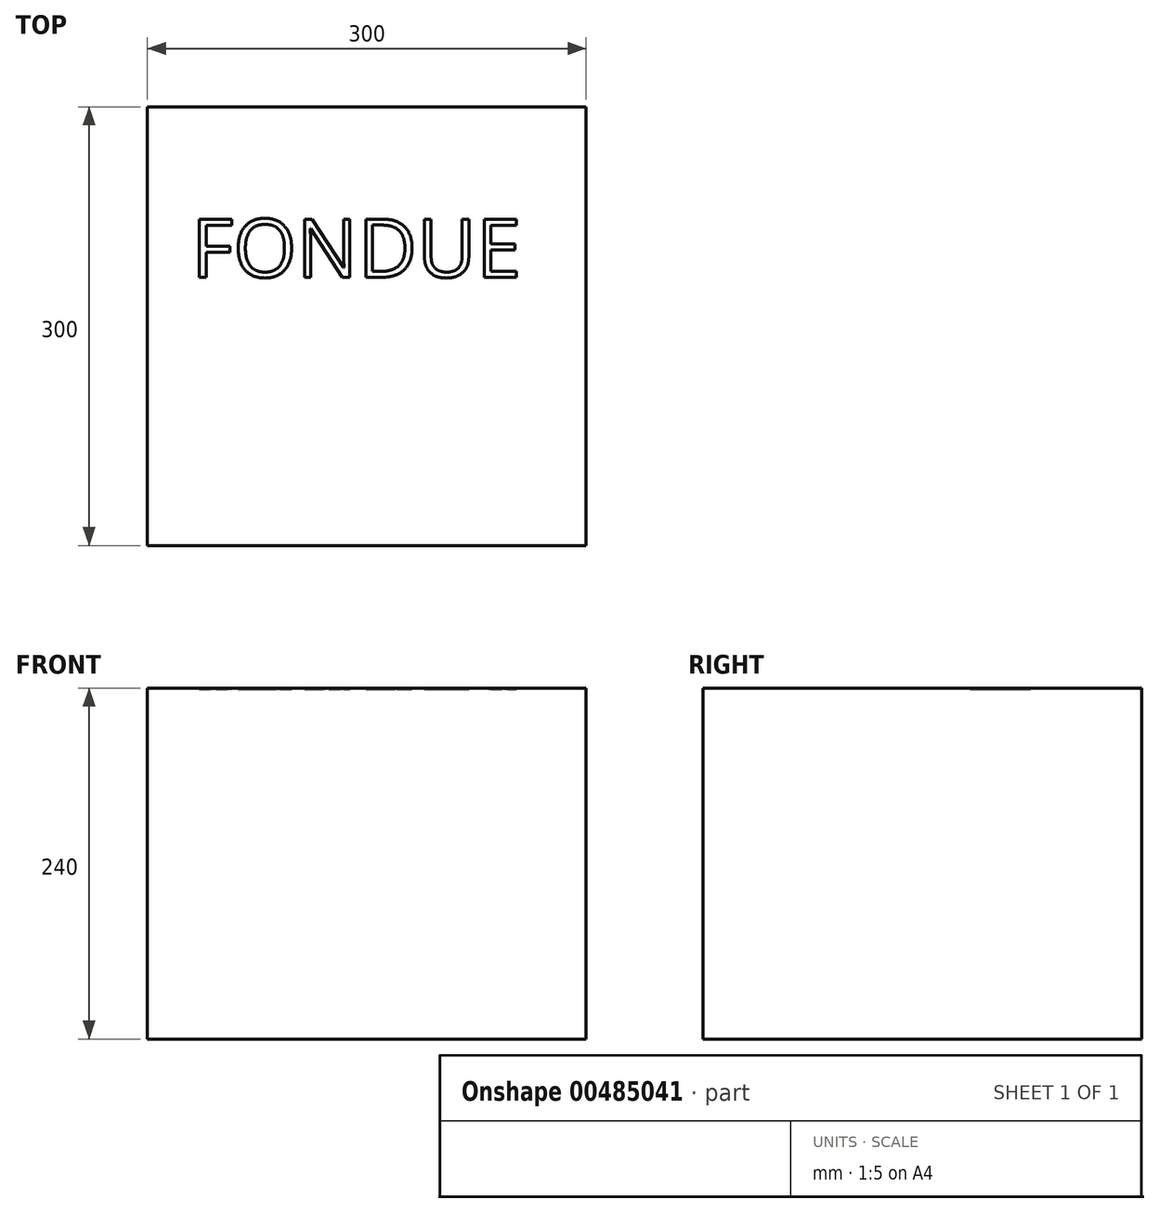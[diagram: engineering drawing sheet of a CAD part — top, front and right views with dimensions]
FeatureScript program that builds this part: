
annotation { "Feature Type Name" : "Feature", "Feature Type Description" : "" }
export const myFeature = defineFeature(function(context is Context, id is Id, definition is map)
    precondition{}
    {
        {
            var Q0;
            Q0=qCreatedBy(makeId("Top.planeOp"),FACE);
            var sketch = newSketch(context, id + "F0", { "sketchPlane" : qUnion([Q0])});
            skLineSegment(sketch, "E0.bottom", {"start": v(-150, -150) * mm, "end": v(150, -150) * mm});
            skLineSegment(sketch, "E0.top", {"start": v(-150, 150) * mm, "end": v(150, 150) * mm});
            skLineSegment(sketch, "E0.left", {"start": v(-150, -150) * mm, "end": v(-150, 150) * mm});
            skLineSegment(sketch, "E0.right", {"start": v(150, -150) * mm, "end": v(150, 150) * mm});
            skPoint(sketch, "E0.middle", {"position": v(0, 0) * mm});
            skSolve(sketch);
        }
        {
            var Q0;
            Q0 = qSketchRegion(id + "F0", true);
            extrude(context, id + "F1", {"entities" : qUnion([Q0]), "depth" : 240 * mm});
        }
        {
            var Q0;
            Q0=makeQuery(id+"F1.opExtrude","CAP_FACE",FACE,{"disambiguationData":[OSD([sQuery(id+"F0.wireOp",EDGE,"E0.bottom"),sQuery(id+"F0.wireOp",EDGE,"E0.top"),sQuery(id+"F0.wireOp",EDGE,"E0.left"),sQuery(id+"F0.wireOp",EDGE,"E0.right")])],"isStart":false});
            var sketch = newSketch(context, id + "F2", { "sketchPlane" : qUnion([Q0])});
            skText(sketch, "E1", { "text": "FONDUE", "fontName": "OpenSans-Regular.ttf"});
            const initialGuessF2  = {"E1": [-0.12, 0.03346, 1, 0, 0.04]};
            skSetInitialGuess(sketch, initialGuessF2);
            skSolve(sketch);
        }
        {
            var Q0;
            Q0 = qSketchRegion(id + "F2", true);
            extrude(context, id + "F3", {"entities" : qUnion([Q0]), "operationType" : NewBodyOperationType.REMOVE, "oppositeDirection" : true, "depth" : 1 * mm});
        }
    });
